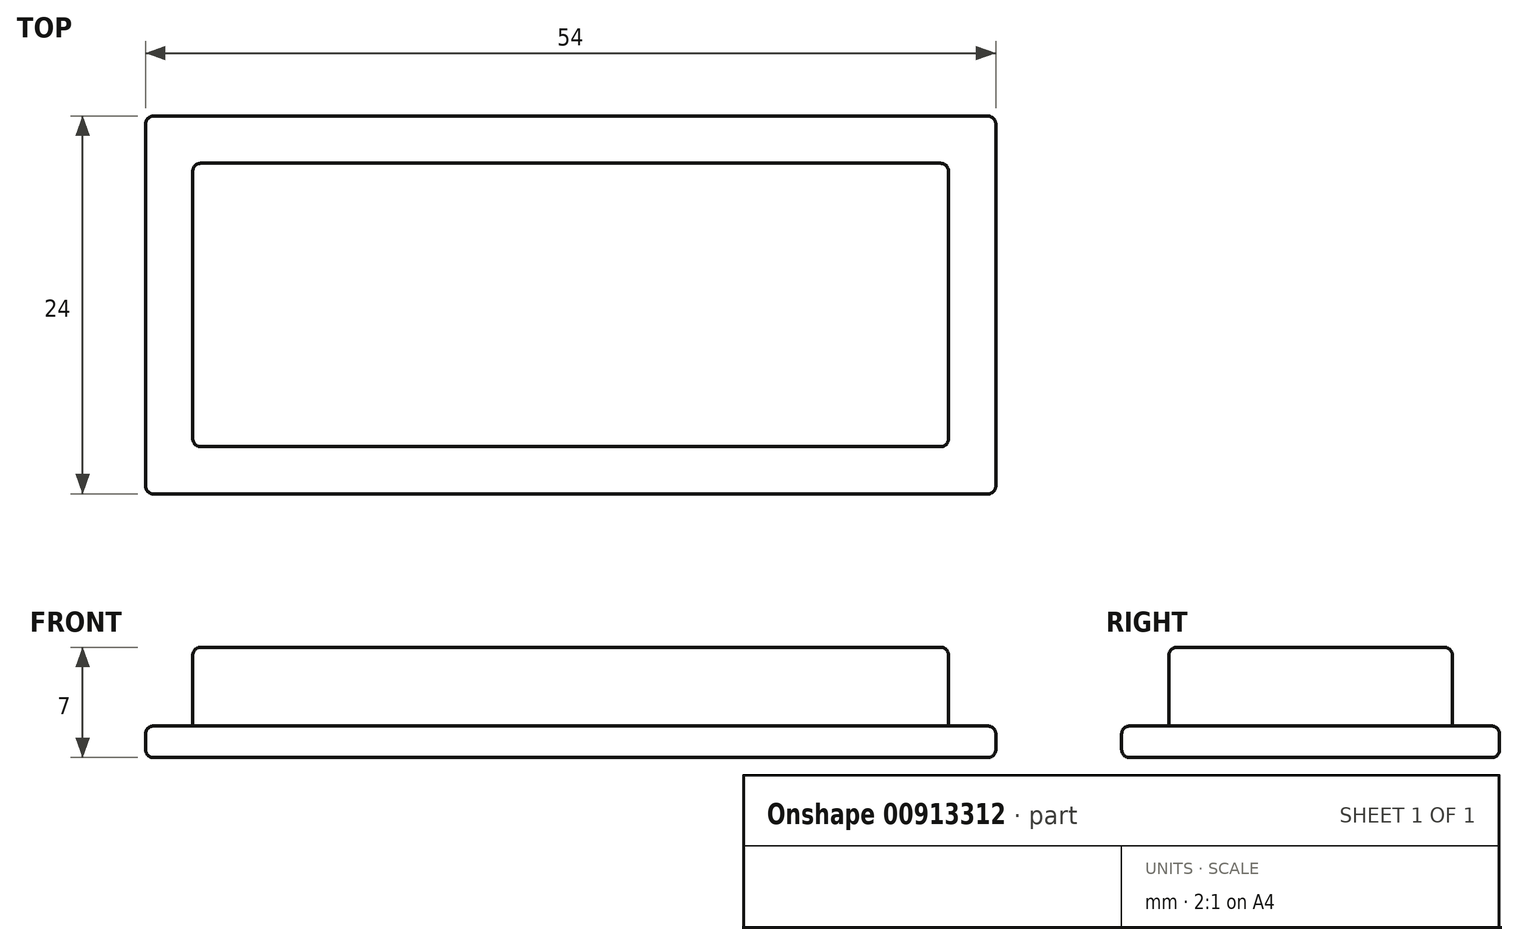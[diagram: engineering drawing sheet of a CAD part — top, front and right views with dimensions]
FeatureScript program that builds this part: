
annotation { "Feature Type Name" : "Feature", "Feature Type Description" : "" }
export const myFeature = defineFeature(function(context is Context, id is Id, definition is map)
    precondition{}
    {
        {
            var Q0;
            Q0=qCreatedBy(makeId("Top.planeOp"),FACE);
            var sketch = newSketch(context, id + "F0", { "sketchPlane" : qUnion([Q0])});
            skLineSegment(sketch, "E0.bottom", {"start": v(-67.4, 42.13) * mm, "end": v(-13.4, 42.13) * mm});
            skLineSegment(sketch, "E0.top", {"start": v(-67.4, 18.13) * mm, "end": v(-13.4, 18.13) * mm});
            skLineSegment(sketch, "E0.left", {"start": v(-67.4, 42.13) * mm, "end": v(-67.4, 18.13) * mm});
            skLineSegment(sketch, "E0.right", {"start": v(-13.4, 42.13) * mm, "end": v(-13.4, 18.13) * mm});
            skSolve(sketch);
        }
        {
            var Q0;
            Q0 = qSketchRegion(id + "F0", true);
            extrude(context, id + "F1", {"entities" : qUnion([Q0]), "depth" : 2 * mm, "offsetDistance" : 25 * mm});
        }
        {
            var Q0;
            Q0=makeQuery(id+"F1.opExtrude","CAP_FACE",FACE,{"disambiguationData":[OSD([sQuery(id+"F0.wireOp",EDGE,"E0.bottom"),sQuery(id+"F0.wireOp",EDGE,"E0.top"),sQuery(id+"F0.wireOp",EDGE,"E0.left"),sQuery(id+"F0.wireOp",EDGE,"E0.right")])],"isStart":false});
            var sketch = newSketch(context, id + "F2", { "sketchPlane" : qUnion([Q0])});
            skLineSegment(sketch, "E1.bottom", {"start": v(-67.4, 42.13) * mm, "end": v(-13.4, 42.13) * mm});
            skLineSegment(sketch, "E1.top", {"start": v(-67.4, 18.13) * mm, "end": v(-13.4, 18.13) * mm});
            skLineSegment(sketch, "E1.left", {"start": v(-67.4, 42.13) * mm, "end": v(-67.4, 18.13) * mm});
            skLineSegment(sketch, "E1.right", {"start": v(-13.4, 42.13) * mm, "end": v(-13.4, 18.13) * mm});
            skLineSegment(sketch, "E2.0", {"start": v(-64.4, 39.13) * mm, "end": v(-64.4, 21.13) * mm});
            skLineSegment(sketch, "E2.1", {"start": v(-16.4, 39.13) * mm, "end": v(-64.4, 39.13) * mm});
            skLineSegment(sketch, "E2.2", {"start": v(-16.4, 21.13) * mm, "end": v(-16.4, 39.13) * mm});
            skLineSegment(sketch, "E2.3", {"start": v(-64.4, 21.13) * mm, "end": v(-16.4, 21.13) * mm});
            skSolve(sketch);
        }
        {
            var Q0;
            Q0=makeQuery(id+"F2.imprint","IMPRINT",FACE,{"disambiguationData":[TD([[makeQuery(id+"F2.imprint","IMPRINT",EDGE,{"derivedFrom":sQuery(id+"F2.wireOp",EDGE,"E2.0")}),1.0]])]});
            extrude(context, id + "F3", {"entities" : qUnion([Q0]), "operationType" : NewBodyOperationType.ADD, "depth" : 5 * mm, "offsetDistance" : 25 * mm});
        }
        {
            var Q0;
            Q0=makeQuery(id+"F3.opExtrude","CAP_EDGE",EDGE,{"disambiguationData":[OSD([sQuery(id+"F2.wireOp",EDGE,"E2.1")])],"isStart":true});
            var Q1;
            Q1=makeQuery(id+"F3.opExtrude","CAP_EDGE",EDGE,{"disambiguationData":[OSD([sQuery(id+"F2.wireOp",EDGE,"E2.1")])],"isStart":false});
            var Q2;
            Q2=makeQuery(id+"F3.opExtrude","SWEPT_EDGE",EDGE,{"disambiguationData":[OSD([sQuery(id+"F2.wireOp",EDGE,"E2.0"),sQuery(id+"F2.wireOp",EDGE,"E2.1")])]});
            var Q3;
            Q3=makeQuery(id+"F3.opExtrude","CAP_EDGE",EDGE,{"disambiguationData":[OSD([sQuery(id+"F2.wireOp",EDGE,"E2.2")])],"isStart":true});
            var Q4;
            Q4=makeQuery(id+"F3.opExtrude","CAP_EDGE",EDGE,{"disambiguationData":[OSD([sQuery(id+"F2.wireOp",EDGE,"E2.2")])],"isStart":false});
            var Q5;
            Q5=makeQuery(id+"F3.opExtrude","CAP_EDGE",EDGE,{"disambiguationData":[OSD([sQuery(id+"F2.wireOp",EDGE,"E2.3")])],"isStart":false});
            var Q6;
            Q6=makeQuery(id+"F3.opExtrude","CAP_EDGE",EDGE,{"disambiguationData":[OSD([sQuery(id+"F2.wireOp",EDGE,"E2.3")])],"isStart":true});
            var Q7;
            Q7=makeQuery(id+"F3.opExtrude","CAP_EDGE",EDGE,{"disambiguationData":[OSD([sQuery(id+"F2.wireOp",EDGE,"E2.0")])],"isStart":false});
            var Q8;
            Q8=makeQuery(id+"F3.opExtrude","CAP_EDGE",EDGE,{"disambiguationData":[OSD([sQuery(id+"F2.wireOp",EDGE,"E2.0")])],"isStart":true});
            var Q9;
            Q9=makeQuery(id+"F3.opExtrude","SWEPT_EDGE",EDGE,{"disambiguationData":[OSD([sQuery(id+"F2.wireOp",EDGE,"E2.0"),sQuery(id+"F2.wireOp",EDGE,"E2.3")])]});
            var Q10;
            Q10=makeQuery(id+"F3.opExtrude","SWEPT_EDGE",EDGE,{"disambiguationData":[OSD([sQuery(id+"F2.wireOp",EDGE,"E2.2"),sQuery(id+"F2.wireOp",EDGE,"E2.3")])]});
            var Q11;
            Q11=makeQuery(id+"F3.opExtrude","SWEPT_EDGE",EDGE,{"disambiguationData":[OSD([sQuery(id+"F2.wireOp",EDGE,"E2.1"),sQuery(id+"F2.wireOp",EDGE,"E2.2")])]});
            var Q12;
            Q12=makeQuery(id+"F1.opExtrude","CAP_EDGE",EDGE,{"disambiguationData":[OSD([sQuery(id+"F0.wireOp",EDGE,"E0.right")])],"isStart":false});
            var Q13;
            Q13=makeQuery(id+"F1.opExtrude","CAP_EDGE",EDGE,{"disambiguationData":[OSD([sQuery(id+"F0.wireOp",EDGE,"E0.right")])],"isStart":true});
            var Q14;
            Q14=makeQuery(id+"F1.opExtrude","SWEPT_EDGE",EDGE,{"disambiguationData":[OSD([sQuery(id+"F0.wireOp",EDGE,"E0.top"),sQuery(id+"F0.wireOp",EDGE,"E0.right")])]});
            var Q15;
            Q15=makeQuery(id+"F1.opExtrude","CAP_EDGE",EDGE,{"disambiguationData":[OSD([sQuery(id+"F0.wireOp",EDGE,"E0.top")])],"isStart":true});
            var Q16;
            Q16=makeQuery(id+"F1.opExtrude","CAP_EDGE",EDGE,{"disambiguationData":[OSD([sQuery(id+"F0.wireOp",EDGE,"E0.top")])],"isStart":false});
            var Q17;
            Q17=makeQuery(id+"F1.opExtrude","CAP_EDGE",EDGE,{"disambiguationData":[OSD([sQuery(id+"F0.wireOp",EDGE,"E0.left")])],"isStart":false});
            var Q18;
            Q18=makeQuery(id+"F1.opExtrude","SWEPT_EDGE",EDGE,{"disambiguationData":[OSD([sQuery(id+"F0.wireOp",EDGE,"E0.top"),sQuery(id+"F0.wireOp",EDGE,"E0.left")])]});
            var Q19;
            Q19=makeQuery(id+"F1.opExtrude","CAP_EDGE",EDGE,{"disambiguationData":[OSD([sQuery(id+"F0.wireOp",EDGE,"E0.left")])],"isStart":true});
            var Q20;
            Q20=makeQuery(id+"F1.opExtrude","SWEPT_EDGE",EDGE,{"disambiguationData":[OSD([sQuery(id+"F0.wireOp",EDGE,"E0.bottom"),sQuery(id+"F0.wireOp",EDGE,"E0.left")])]});
            var Q21;
            Q21=makeQuery(id+"F1.opExtrude","CAP_EDGE",EDGE,{"disambiguationData":[OSD([sQuery(id+"F0.wireOp",EDGE,"E0.bottom")])],"isStart":false});
            var Q22;
            Q22=makeQuery(id+"F1.opExtrude","CAP_EDGE",EDGE,{"disambiguationData":[OSD([sQuery(id+"F0.wireOp",EDGE,"E0.bottom")])],"isStart":true});
            var Q23;
            Q23=makeQuery(id+"F1.opExtrude","SWEPT_EDGE",EDGE,{"disambiguationData":[OSD([sQuery(id+"F0.wireOp",EDGE,"E0.bottom"),sQuery(id+"F0.wireOp",EDGE,"E0.right")])]});
            fillet(context, id + "F4", {"entities" : qUnion([Q0, Q1, Q2, Q3, Q4, Q5, Q6, Q7, Q8, Q9, Q10, Q11, Q12, Q13, Q14, Q15, Q16, Q17, Q18, Q19, Q20, Q21, Q22, Q23]), "radius" : 0.5 * mm, "tangentPropagation" : true, "allowEdgeOverflow" : false});
        }
    });
